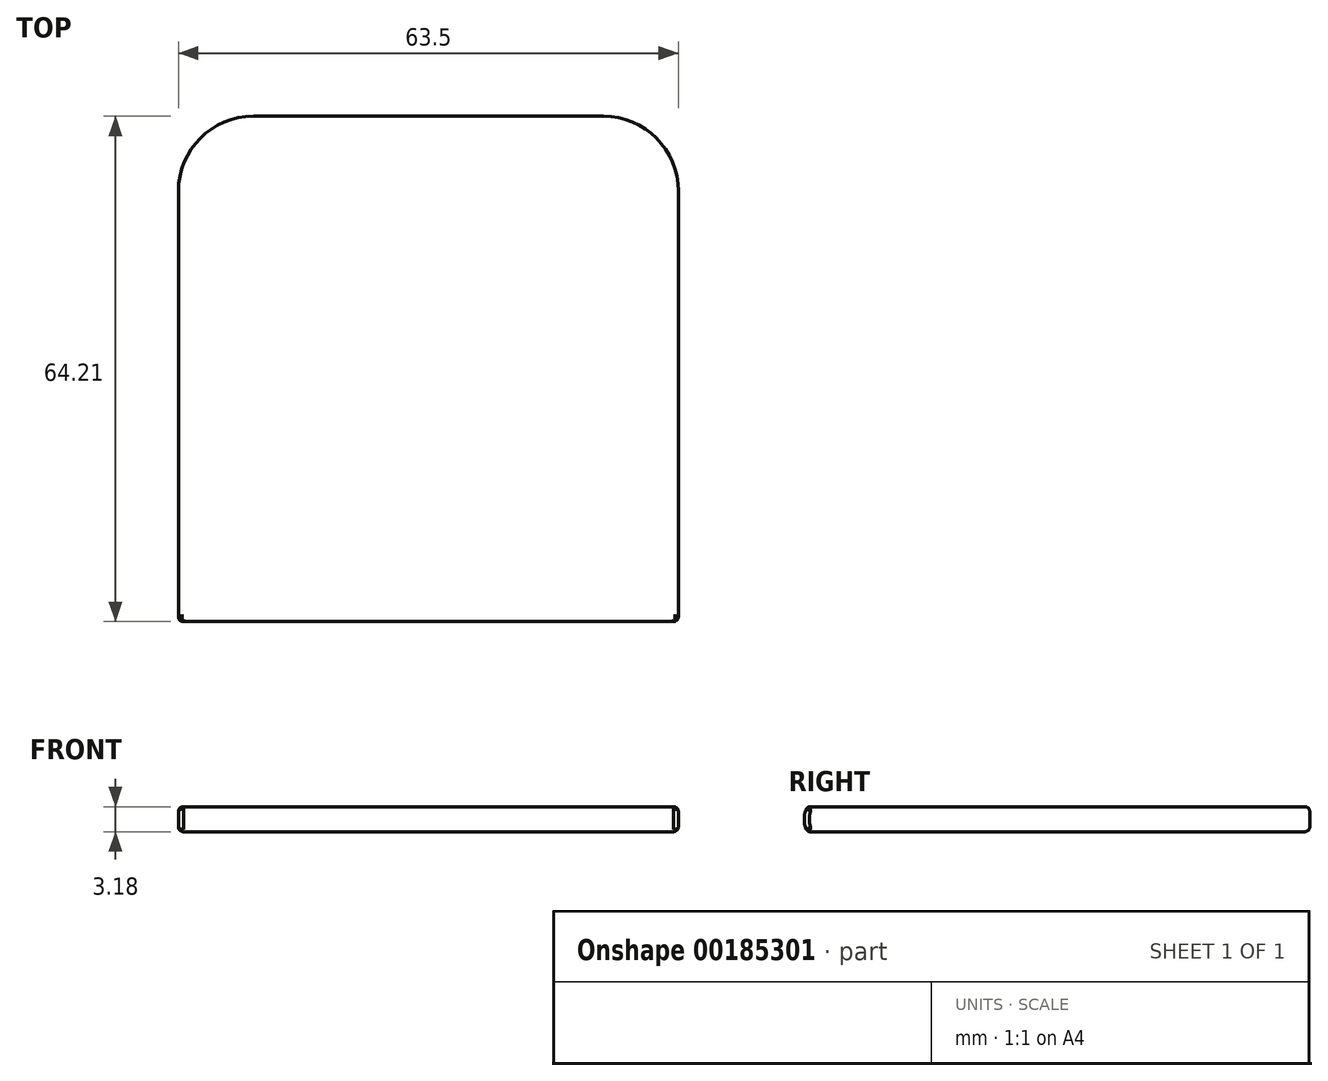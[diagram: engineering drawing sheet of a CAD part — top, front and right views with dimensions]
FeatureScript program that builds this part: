
annotation { "Feature Type Name" : "Feature", "Feature Type Description" : "" }
export const myFeature = defineFeature(function(context is Context, id is Id, definition is map)
    precondition{}
    {
        {
            var Q0;
            Q0=qCreatedBy(makeId("Top.planeOp"),FACE);
            var sketch = newSketch(context, id + "F0", { "sketchPlane" : qUnion([Q0])});
            skLineSegment(sketch, "E0.bottom", {"start": v(0, 0) * mm, "end": v(63.5, 0) * mm});
            skLineSegment(sketch, "E0.top", {"start": v(9.52, 63.5) * mm, "end": v(53.97, 63.5) * mm});
            skLineSegment(sketch, "E0.left", {"start": v(0, 0) * mm, "end": v(0, 53.98) * mm});
            skLineSegment(sketch, "E0.right", {"start": v(63.5, 0) * mm, "end": v(63.5, 53.97) * mm});
            skPoint(sketch, "E1.visualSharp", {"position": v(0, 63.5) * mm});
            skArc(sketch, "E1.filletArc", {"start": v(9.52, 63.5) * mm, "mid": v(2.79, 60.71) * mm, "end": v(0, 53.98) * mm});
            skPoint(sketch, "E2.visualSharp", {"position": v(63.5, 63.5) * mm});
            skArc(sketch, "E2.filletArc", {"start": v(63.5, 53.97) * mm, "mid": v(60.71, 60.71) * mm, "end": v(53.97, 63.5) * mm});
            skPoint(sketch, "E3.visualSharp", {"position": v(0, 0) * mm});
            skLineSegment(sketch, "E3.filletArc", {"start": v(0, 0) * mm, "end": v(0, 0) * mm});
            skPoint(sketch, "E4.visualSharp", {"position": v(63.5, 0) * mm});
            skLineSegment(sketch, "E4.filletArc", {"start": v(63.5, 0) * mm, "end": v(63.5, 0) * mm});
            skSolve(sketch);
        }
        {
            var Q0;
            Q0=makeQuery(id+"F0.imprint","IMPRINT",FACE,{"disambiguationData":[TD([[makeQuery(id+"F0.imprint","IMPRINT",EDGE,{"derivedFrom":sQuery(id+"F0.wireOp",EDGE,"E0.bottom")}),1.0]])]});
            extrude(context, id + "F1", {"entities" : qUnion([Q0]), "depth" : 3.17 * mm});
        }
        {
            var Q0;
            Q0=makeQuery(id+"F1.opExtrude","SWEPT_FACE",FACE,{"disambiguationData":[OSD([sQuery(id+"F0.wireOp",EDGE,"E0.right")])]});
            var sketch = newSketch(context, id + "F2", { "sketchPlane" : qUnion([Q0])});
            skFitSpline(sketch, "E5", {"points": [v(0, 3.18) * mm, v(-0.57, 2.58) * mm, v(-0.57, 0.6) * mm, v(0, 0) * mm], "startDerivative": vector(-2.73, 0) * mm, "endDerivative": vector(2.73, 0) * mm});
            skLineSegment(sketch, "E6", {"start": v(0, 1.59) * mm, "end": v(-0.71, 1.59) * mm, "construction": true});
            skLineSegment(sketch, "E7", {"start": v(-0.57, 2.58) * mm, "end": v(-0.57, 0.6) * mm, "construction": true});
            skPoint(sketch, "E8", {"position": v(-0.57, 1.59) * mm});
            skLineSegment(sketch, "E9", {"start": v(-0.26, 3.18) * mm, "end": v(-0.26, 0) * mm, "construction": true});
            skPoint(sketch, "E10", {"position": v(-0.26, 1.59) * mm});
            skSolve(sketch);
        }
        {
            var Q0;
            Q0=makeQuery(id+"F2.imprint","IMPRINT",FACE,{"disambiguationData":[TD([[makeQuery(id+"F2.imprint","IMPRINT",EDGE,{"derivedFrom":sQuery(id+"F2.wireOp",EDGE,"E5")}),1.0]])]});
            var Q1;
            Q1=makeQuery(id+"F1.opExtrude","SWEPT_FACE",FACE,{"disambiguationData":[OSD([sQuery(id+"F0.wireOp",EDGE,"E0.left")])]});
            extrude(context, id + "F3", {"entities" : qUnion([Q0]), "operationType" : NewBodyOperationType.ADD, "endBound" : BoundingType.UP_TO_SURFACE, "oppositeDirection" : true, "endBoundEntityFace" : qUnion([Q1]), "depth" : 25.4 * mm});
        }
        {
            var Q0;
            Q0=makeQuery(id+"F1.opExtrude","SWEPT_FACE",FACE,{"disambiguationData":[OSD([sQuery(id+"F0.wireOp",EDGE,"E0.top")])]});
            fillet(context, id + "F4", {"entities" : qUnion([Q0]), "radius" : 0.64 * mm, "tangentPropagation" : true, "allowEdgeOverflow" : false});
        }
    });
